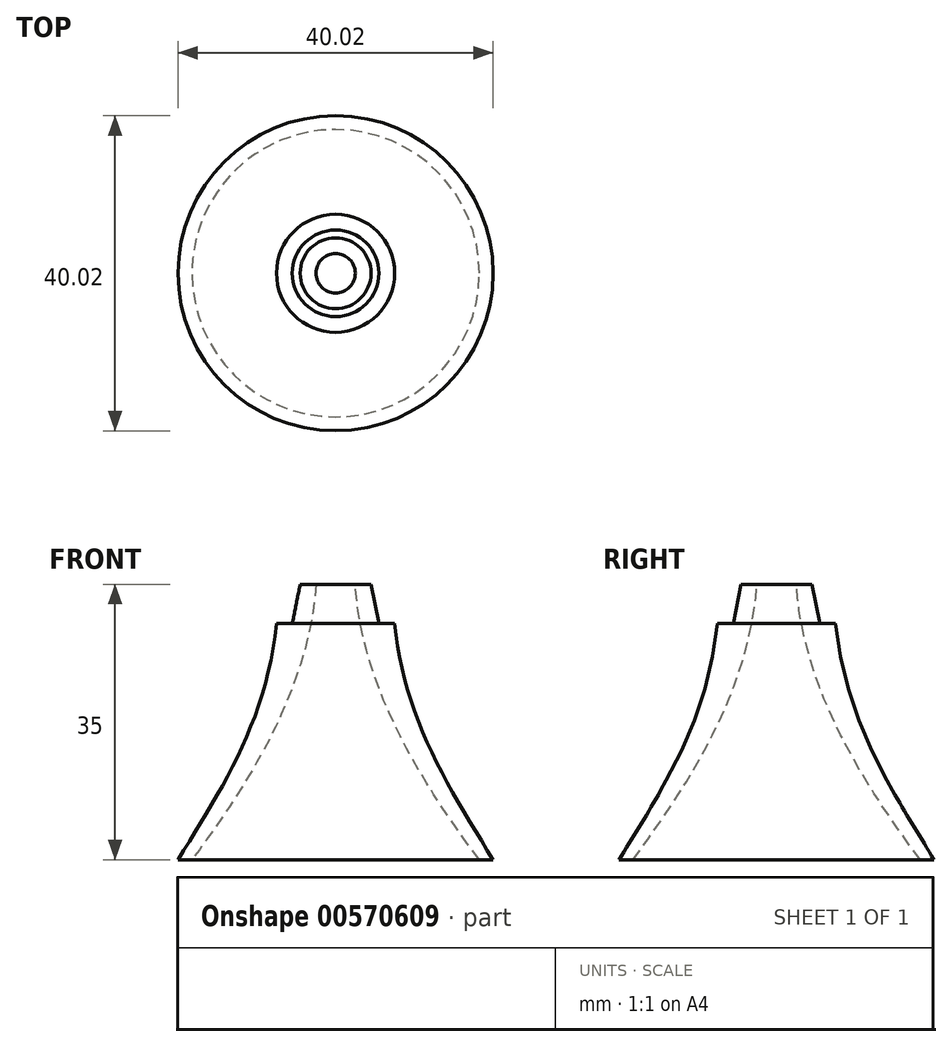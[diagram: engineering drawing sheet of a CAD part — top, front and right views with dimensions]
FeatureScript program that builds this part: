
annotation { "Feature Type Name" : "Feature", "Feature Type Description" : "" }
export const myFeature = defineFeature(function(context is Context, id is Id, definition is map)
    precondition{}
    {
        {
            var Q0;
            Q0=qCreatedBy(makeId("Front.planeOp"),FACE);
            var sketch = newSketch(context, id + "F0", { "sketchPlane" : qUnion([Q0])});
            skLineSegment(sketch, "E0", {"start": v(7.5, 30) * mm, "end": v(5.5, 30) * mm});
            skLineSegment(sketch, "E1", {"start": v(5.5, 30) * mm, "end": v(4.5, 35) * mm});
            skLineSegment(sketch, "E2", {"start": v(4.5, 35) * mm, "end": v(2.5, 35) * mm});
            skLineSegment(sketch, "E3", {"start": v(0, 0) * mm, "end": v(20, 0) * mm});
            skFitSpline(sketch, "E4", {"points": [v(7.5, 30) * mm, v(20, 0) * mm], "startDerivative": vector(3.88, -37.39) * mm, "endDerivative": vector(16.47, -27.03) * mm});
            skFitSpline(sketch, "E5", {"points": [v(2.5, 35) * mm, v(18.25, 0) * mm], "startDerivative": vector(2.76, -40.12) * mm, "endDerivative": vector(21.73, -29.13) * mm});
            skSolve(sketch);
        }
        {
            var Q0;
            Q0=qCreatedBy(makeId("Front.planeOp"),FACE);
            var sketch = newSketch(context, id + "F1", { "sketchPlane" : qUnion([Q0])});
            skLineSegment(sketch, "E6", {"start": v(0, 12.27) * mm, "end": v(0, 23.3) * mm});
            skSolve(sketch);
        }
        {
            var Q0;
            Q0=makeQuery(id+"F0.imprint","IMPRINT",FACE,{"disambiguationData":[TD([[makeQuery(id+"F0.imprint","IMPRINT",EDGE,{"derivedFrom":sQuery(id+"F0.wireOp",EDGE,"E0")}),1.0]])]});
            var Q1;
            Q1=sQuery(id+"F1.wireOp",EDGE,"E6");
            revolve(context, id + "F2", {"entities" : qUnion([Q0]), "axis" : qUnion([Q1]), "revolveType" : RevolveType.FULL});
        }
    });
